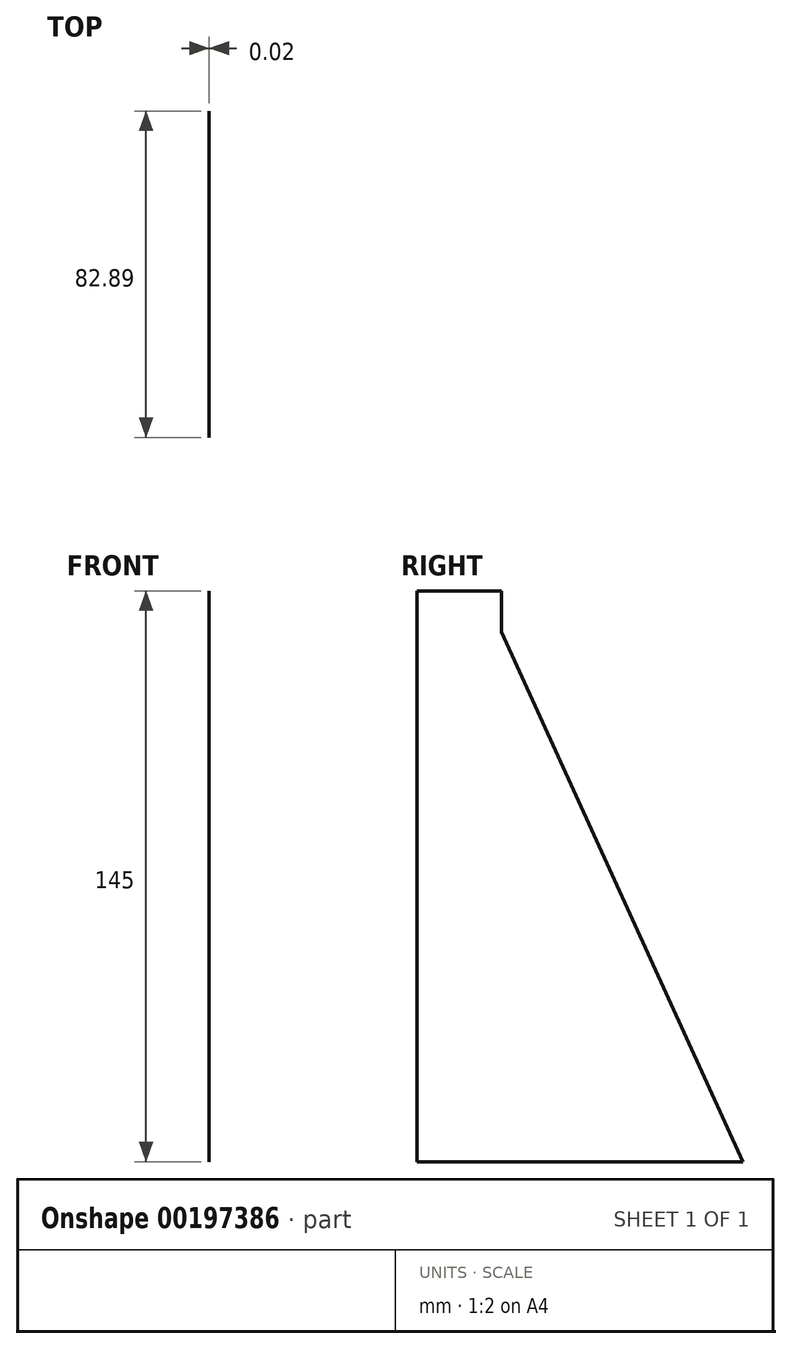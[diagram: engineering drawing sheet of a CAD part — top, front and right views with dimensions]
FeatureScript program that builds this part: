
annotation { "Feature Type Name" : "Feature", "Feature Type Description" : "" }
export const myFeature = defineFeature(function(context is Context, id is Id, definition is map)
    precondition{}
    {
        {
            var Q0;
            Q0=qCreatedBy(makeId("Right.planeOp"),FACE);
            var sketch = newSketch(context, id + "F0", { "sketchPlane" : qUnion([Q0])});
            skLineSegment(sketch, "E0", {"start": v(0, 62.83) * mm, "end": v(21.5, 62.83) * mm});
            skLineSegment(sketch, "E1", {"start": v(82.89, -82.17) * mm, "end": v(0, -82.17) * mm});
            skLineSegment(sketch, "E2", {"start": v(0, -82.17) * mm, "end": v(0, 62.83) * mm});
            skLineSegment(sketch, "E3", {"start": v(21.5, 62.83) * mm, "end": v(21.5, 52.46) * mm});
            skLineSegment(sketch, "E4", {"start": v(21.5, 52.46) * mm, "end": v(82.89, -82.17) * mm});
            skSolve(sketch);
        }
        {
            var Q0;
            Q0 = qSketchRegion(id + "F0", true);
            extrude(context, id + "F1", {"entities" : qUnion([Q0]), "endBound" : BoundingType.SYMMETRIC, "depth" : 3 / 203.2 * mm});
        }
    });
